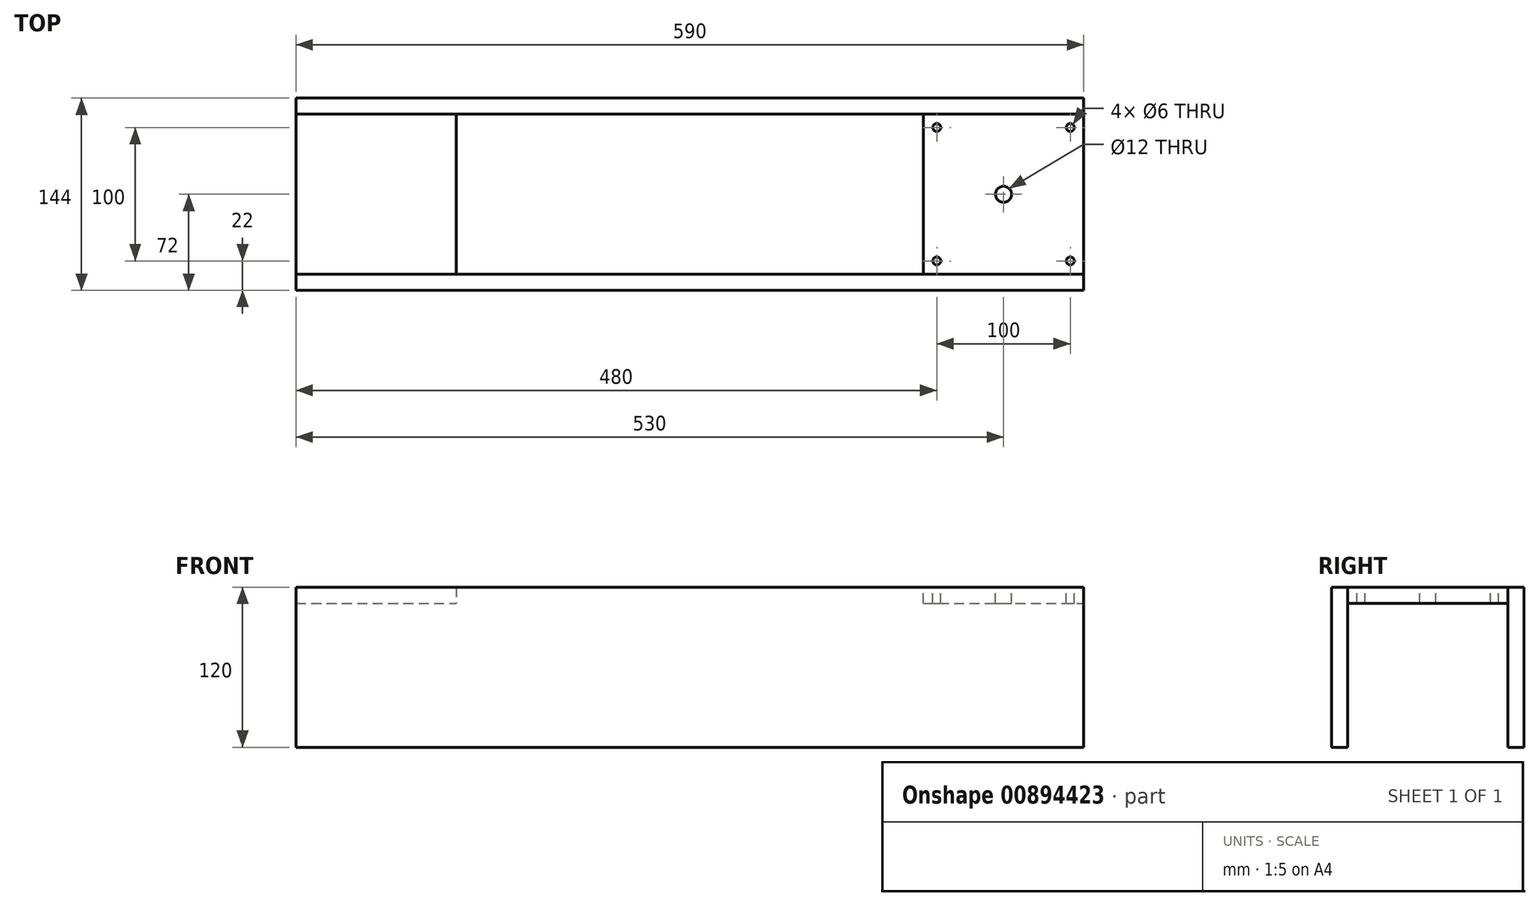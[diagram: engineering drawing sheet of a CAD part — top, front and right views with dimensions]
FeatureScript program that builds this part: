
annotation { "Feature Type Name" : "Feature", "Feature Type Description" : "" }
export const myFeature = defineFeature(function(context is Context, id is Id, definition is map)
    precondition{}
    {
        {
            var Q0;
            Q0=qCreatedBy(makeId("Front.planeOp"),FACE);
            var sketch = newSketch(context, id + "F0", { "sketchPlane" : qUnion([Q0])});
            skLineSegment(sketch, "E0.bottom", {"start": v(-60, -6) * mm, "end": v(60, -6) * mm});
            skLineSegment(sketch, "E0.top", {"start": v(-60, 6) * mm, "end": v(60, 6) * mm});
            skLineSegment(sketch, "E0.left", {"start": v(-60, -6) * mm, "end": v(-60, 6) * mm});
            skLineSegment(sketch, "E0.right", {"start": v(60, -6) * mm, "end": v(60, 6) * mm});
            skPoint(sketch, "E0.middle", {"position": v(0, 0) * mm});
            skSolve(sketch);
        }
        {
            var Q0;
            Q0 = qSketchRegion(id + "F0", true);
            extrude(context, id + "F1", {"entities" : qUnion([Q0]), "oppositeDirection" : true, "depth" : 120 * mm, "offsetDistance" : 25 * mm});
        }
        {
            var Q0;
            Q0=qCreatedBy(makeId("Front.planeOp"),FACE);
            var sketch = newSketch(context, id + "F2", { "sketchPlane" : qUnion([Q0])});
            skLineSegment(sketch, "E1.bottom", {"start": v(-530, 6) * mm, "end": v(60, 6) * mm});
            skLineSegment(sketch, "E1.top", {"start": v(-530, -114) * mm, "end": v(60, -114) * mm});
            skLineSegment(sketch, "E1.left", {"start": v(-530, 6) * mm, "end": v(-530, -114) * mm});
            skLineSegment(sketch, "E1.right", {"start": v(60, 6) * mm, "end": v(60, -114) * mm});
            skSolve(sketch);
        }
        {
            var Q0;
            Q0 = qSketchRegion(id + "F2", true);
            extrude(context, id + "F3", {"entities" : qUnion([Q0]), "depth" : 12 * mm, "offsetDistance" : 25 * mm});
        }
        {
            var Q0;
            Q0=qCreatedBy(makeId("Front.planeOp"),FACE);
            var sketch = newSketch(context, id + "F4", { "sketchPlane" : qUnion([Q0])});
            skLineSegment(sketch, "E2.bottom", {"start": v(-530, 6) * mm, "end": v(-410, 6) * mm});
            skLineSegment(sketch, "E2.top", {"start": v(-530, -6) * mm, "end": v(-410, -6) * mm});
            skLineSegment(sketch, "E2.left", {"start": v(-530, 6) * mm, "end": v(-530, -6) * mm});
            skLineSegment(sketch, "E2.right", {"start": v(-410, 6) * mm, "end": v(-410, -6) * mm});
            skSolve(sketch);
        }
        {
            var Q0;
            Q0 = qSketchRegion(id + "F4", true);
            extrude(context, id + "F5", {"entities" : qUnion([Q0]), "oppositeDirection" : true, "depth" : 120 * mm, "offsetDistance" : 25 * mm});
        }
        {
            var Q0;
            Q0=makeQuery(id+"F1.opExtrude","CAP_FACE",FACE,{"disambiguationData":[OSD([sQuery(id+"F0.wireOp",EDGE,"E0.bottom"),sQuery(id+"F0.wireOp",EDGE,"E0.top"),sQuery(id+"F0.wireOp",EDGE,"E0.left"),sQuery(id+"F0.wireOp",EDGE,"E0.right")])],"isStart":false});
            var sketch = newSketch(context, id + "F6", { "sketchPlane" : qUnion([Q0])});
            skLineSegment(sketch, "E3.bottom", {"start": v(-60, 6) * mm, "end": v(530, 6) * mm});
            skLineSegment(sketch, "E3.top", {"start": v(-60, -114) * mm, "end": v(530, -114) * mm});
            skLineSegment(sketch, "E3.left", {"start": v(-60, 6) * mm, "end": v(-60, -114) * mm});
            skLineSegment(sketch, "E3.right", {"start": v(530, 6) * mm, "end": v(530, -114) * mm});
            skSolve(sketch);
        }
        {
            var Q0;
            Q0 = qSketchRegion(id + "F6", true);
            extrude(context, id + "F7", {"entities" : qUnion([Q0]), "depth" : 12 * mm, "offsetDistance" : 25 * mm});
        }
        {
            var Q0;
            Q0=makeQuery(id+"F1.opExtrude","SWEPT_FACE",FACE,{"disambiguationData":[OSD([sQuery(id+"F0.wireOp",EDGE,"E0.top")])]});
            var sketch = newSketch(context, id + "F8", { "sketchPlane" : qUnion([Q0])});
            skCircle(sketch, "E4", {"center": v(0, 60) * mm, "radius": 6 * mm});
            skPoint(sketch, "E4.centerSnap0", {"position": v(-60, 60) * mm});
            skPoint(sketch, "E4.centerSnap1", {"position": v(0, 0) * mm});
            skLineSegment(sketch, "E5.bottom", {"start": v(50, 10) * mm, "end": v(-50, 10) * mm, "construction": true});
            skLineSegment(sketch, "E5.top", {"start": v(50, 110) * mm, "end": v(-50, 110) * mm, "construction": true});
            skLineSegment(sketch, "E5.left", {"start": v(50, 10) * mm, "end": v(50, 110) * mm, "construction": true});
            skLineSegment(sketch, "E5.right", {"start": v(-50, 10) * mm, "end": v(-50, 110) * mm, "construction": true});
            skCircle(sketch, "E6", {"center": v(-50, 110) * mm, "radius": 3 * mm});
            skCircle(sketch, "E7", {"center": v(50, 110) * mm, "radius": 3 * mm});
            skCircle(sketch, "E8", {"center": v(50, 10) * mm, "radius": 3 * mm});
            skCircle(sketch, "E9", {"center": v(-50, 10) * mm, "radius": 3 * mm});
            skSolve(sketch);
        }
        {
            var Q0;
            Q0=makeQuery(id+"F8.imprint","IMPRINT",FACE,{"disambiguationData":[TD([[makeQuery(id+"F8.imprint","IMPRINT",EDGE,{"derivedFrom":sQuery(id+"F8.wireOp",EDGE,"E7")}),1.0]])]});
            var Q1;
            Q1=makeQuery(id+"F8.imprint","IMPRINT",FACE,{"disambiguationData":[TD([[makeQuery(id+"F8.imprint","IMPRINT",EDGE,{"derivedFrom":sQuery(id+"F8.wireOp",EDGE,"E6")}),1.0]])]});
            var Q2;
            Q2=makeQuery(id+"F8.imprint","IMPRINT",FACE,{"disambiguationData":[TD([[makeQuery(id+"F8.imprint","IMPRINT",EDGE,{"derivedFrom":sQuery(id+"F8.wireOp",EDGE,"E9")}),1.0]])]});
            var Q3;
            Q3=makeQuery(id+"F8.imprint","IMPRINT",FACE,{"disambiguationData":[TD([[makeQuery(id+"F8.imprint","IMPRINT",EDGE,{"derivedFrom":sQuery(id+"F8.wireOp",EDGE,"E4")}),1.0]])]});
            var Q4;
            Q4=makeQuery(id+"F8.imprint","IMPRINT",FACE,{"disambiguationData":[TD([[makeQuery(id+"F8.imprint","IMPRINT",EDGE,{"derivedFrom":sQuery(id+"F8.wireOp",EDGE,"E8")}),1.0]])]});
            extrude(context, id + "F9", {"entities" : qUnion([Q0, Q1, Q2, Q3, Q4]), "operationType" : NewBodyOperationType.REMOVE, "endBound" : BoundingType.THROUGH_ALL, "oppositeDirection" : true, "depth" : 25 * mm, "offsetDistance" : 25 * mm});
        }
    });
